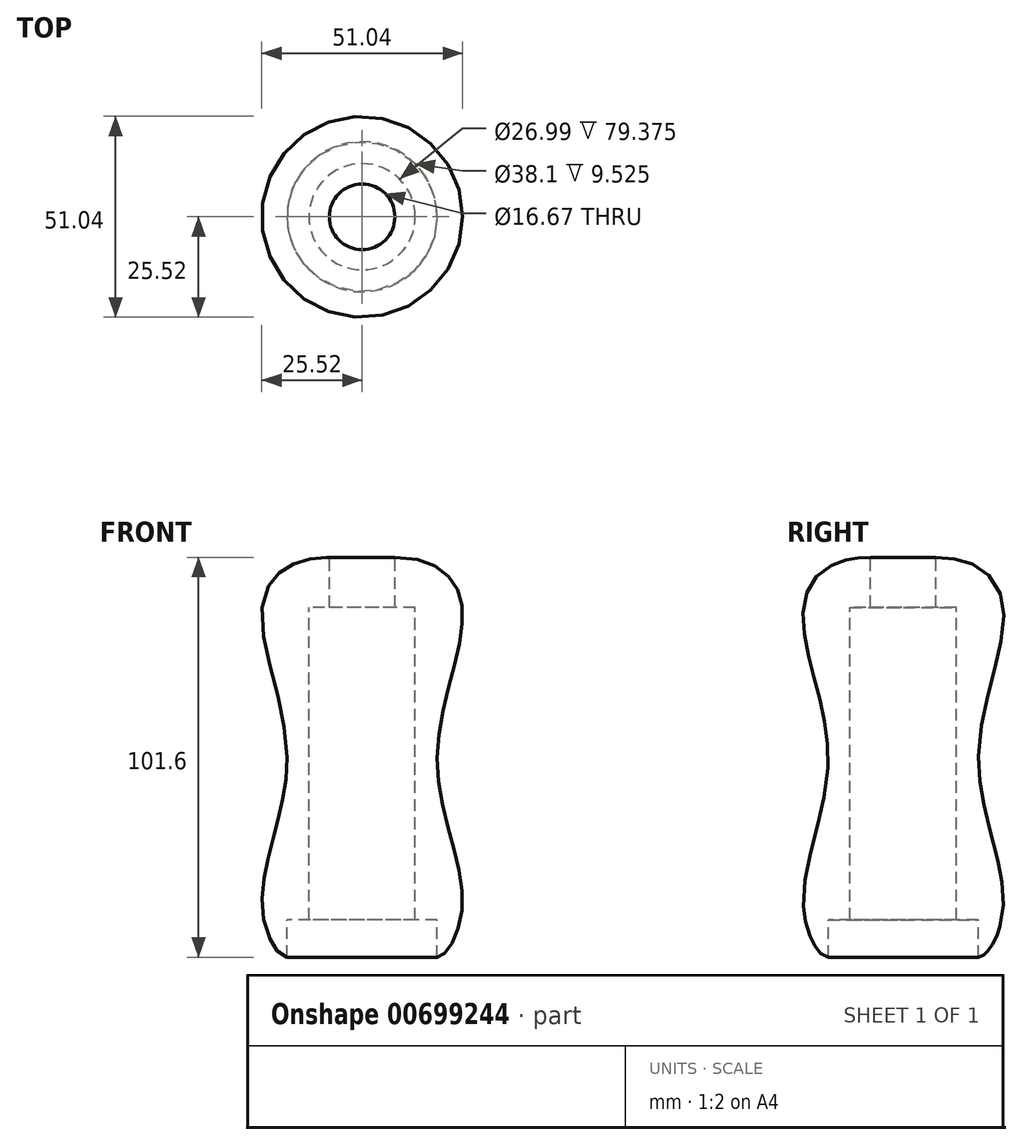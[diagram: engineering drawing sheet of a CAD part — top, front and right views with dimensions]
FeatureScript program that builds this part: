
annotation { "Feature Type Name" : "Feature", "Feature Type Description" : "" }
export const myFeature = defineFeature(function(context is Context, id is Id, definition is map)
    precondition{}
    {
        {
            var Q0;
            Q0=qCreatedBy(makeId("Front.planeOp"),FACE);
            var sketch = newSketch(context, id + "F0", { "sketchPlane" : qUnion([Q0])});
            skLineSegment(sketch, "E0", {"start": v(0, 50.8) * mm, "end": v(-8.33, 50.8) * mm});
            skLineSegment(sketch, "E1", {"start": v(-8.33, 50.8) * mm, "end": v(-8.33, 38.1) * mm});
            skLineSegment(sketch, "E2", {"start": v(-8.33, 38.1) * mm, "end": v(-13.5, 38.1) * mm});
            skLineSegment(sketch, "E3", {"start": v(-13.5, 38.1) * mm, "end": v(-13.5, -41.27) * mm});
            skLineSegment(sketch, "E4", {"start": v(-13.5, -41.27) * mm, "end": v(-19.05, -41.27) * mm});
            skLineSegment(sketch, "E5", {"start": v(-19.05, -41.27) * mm, "end": v(-19.05, -50.8) * mm});
            skLineSegment(sketch, "E6", {"start": v(-19.05, -50.8) * mm, "end": v(0, -50.8) * mm});
            skLineSegment(sketch, "E7", {"start": v(0, 50.8) * mm, "end": v(0, -50.8) * mm, "construction": true});
            skLineSegment(sketch, "E8.bottom", {"start": v(0, 50.8) * mm, "end": v(-38.1, 50.8) * mm, "construction": true});
            skLineSegment(sketch, "E8.top", {"start": v(0, -50.8) * mm, "end": v(-38.1, -50.8) * mm, "construction": true});
            skLineSegment(sketch, "E8.left", {"start": v(0, 50.8) * mm, "end": v(0, -50.8) * mm});
            skLineSegment(sketch, "E8.right", {"start": v(-38.1, 50.8) * mm, "end": v(-38.1, -50.8) * mm, "construction": true});
            skLineSegment(sketch, "E9.MirrorCS", {"start": v(8.33, 38.1) * mm, "end": v(13.5, 38.1) * mm});
            skLineSegment(sketch, "E10.MirrorCS", {"start": v(13.5, -41.27) * mm, "end": v(19.05, -41.27) * mm});
            skLineSegment(sketch, "E11.MirrorCS", {"start": v(0, 50.8) * mm, "end": v(8.33, 50.8) * mm});
            skLineSegment(sketch, "E12.MirrorCS", {"start": v(19.05, -50.8) * mm, "end": v(0, -50.8) * mm});
            skLineSegment(sketch, "E13.MirrorCS", {"start": v(13.5, 38.1) * mm, "end": v(13.5, -41.27) * mm});
            skLineSegment(sketch, "E14.MirrorCS", {"start": v(8.33, 50.8) * mm, "end": v(8.33, 38.1) * mm});
            skLineSegment(sketch, "E15.MirrorCS", {"start": v(38.1, 50.8) * mm, "end": v(38.1, -50.8) * mm, "construction": true});
            skLineSegment(sketch, "E16.MirrorCS", {"start": v(19.05, -41.27) * mm, "end": v(19.05, -50.8) * mm});
            skLineSegment(sketch, "E17.MirrorCS", {"start": v(0, 50.8) * mm, "end": v(38.1, 50.8) * mm, "construction": true});
            skLineSegment(sketch, "E18.MirrorCS", {"start": v(0, -50.8) * mm, "end": v(38.1, -50.8) * mm, "construction": true});
            skFitSpline(sketch, "E19", {"points": [v(8.33, 50.8) * mm, v(25.4, 38.1) * mm, v(19.05, 0) * mm, v(25.4, -38.1) * mm, v(19.05, -50.8) * mm], "startDerivative": vector(145.05, 0) * mm, "endDerivative": vector(-42.08, 0) * mm});
            skSolve(sketch);
        }
        {
            var Q0;
            Q0=makeQuery(id+"F0.imprint","IMPRINT",FACE,{"disambiguationData":[TD([[makeQuery(id+"F0.imprint","IMPRINT",EDGE,{"derivedFrom":sQuery(id+"F0.wireOp",EDGE,"E9.MirrorCS")}),1.0]])]});
            var Q1;
            Q1=sQuery(id+"F0.wireOp",EDGE,"E8.left");
            revolve(context, id + "F1", {"entities" : qUnion([Q0]), "axis" : qUnion([Q1]), "revolveType" : RevolveType.FULL});
        }
    });
